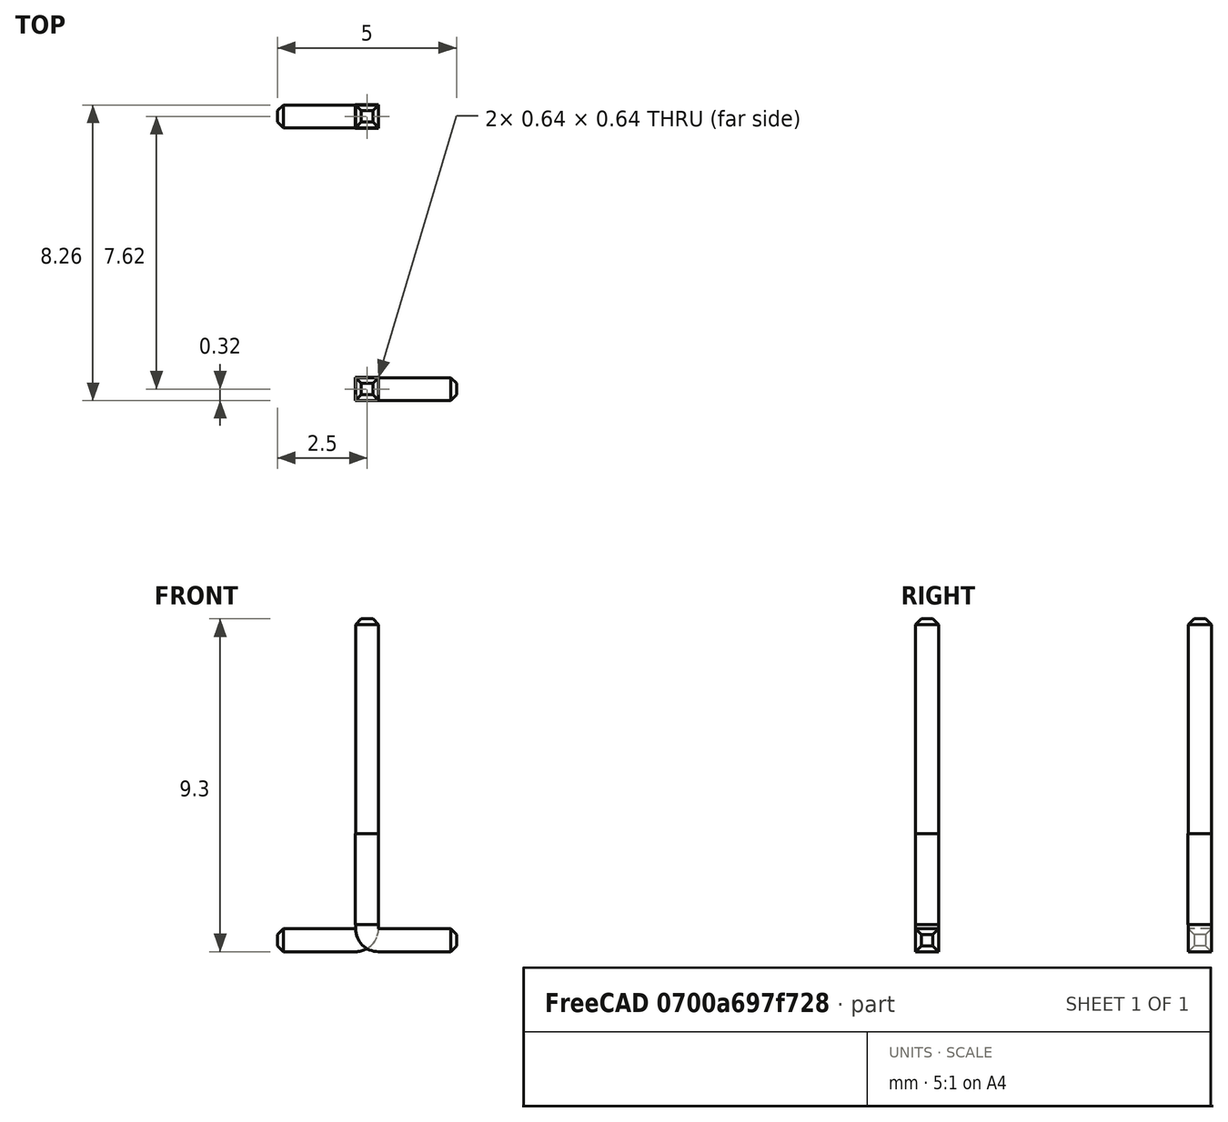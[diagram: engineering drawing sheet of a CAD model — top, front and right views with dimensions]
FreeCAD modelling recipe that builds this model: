
FCSTD DOCUMENT  (FreeCAD 0.16R6712 (Git))
Label: Pin_Neo
License: All rights reserved
LicenseURL: http://en.wikipedia.org/wiki/All_rights_reserved
objects: Part::Box×5, Part::Cut×5, Part::Feature×1, Part::FeaturePython×1
note: 12 computed .brp shape members not serialized (recipe doc carries the construction recipe); baked Part::Feature solids carry a one-line shape summary decoded from their .brp

FEATURE [Part::Feature] Part__Feature  label="PinHeader_1x04_P254mm_Vertical_SMD_Pin1Left"
  shape: bbox 5 x 10.16 x 9.3 mm, 112 faces (baked)
FEATURE [Part::Box] Box  label="Cube"
  Height = 12
  Length = 8
  Placement = pos=(-4,-3.48,-1) rot=(0,0,1;0rad)
  Width = 6.96
FEATURE [Part::Cut] Cut
  Base = -> Part__Feature
  Tool = -> Box
FEATURE [Part::FeaturePython] Clone  label="Clone of Cut"  # Draft clone (typed FeaturePython)
  Objects = -> [Cut]
  Scale = (1,1,1)
FEATURE [Part::Box] Box001  label="Cube001"
  Height = 10
  Length = 1.2
  Placement = pos=(0.321,-6,0.65) rot=(0,0,1;0rad)
  Width = 12
FEATURE [Part::Box] Box002  label="Cube002"
  Height = 10
  Length = 1.2
  Placement = pos=(-1.529,-6,0.65) rot=(0,0,1;0rad)
  Width = 12
FEATURE [Part::Box] Box003  label="Cube003"
  Height = 10
  Length = 3
  Placement = pos=(-1.529,-6,0.65) rot=(0,0,1;0rad)
  Width = 1.868
FEATURE [Part::Box] Box004  label="Cube004"
  Height = 10
  Length = 3
  Placement = pos=(-1.529,4.134,0.4) rot=(0,0,1;0rad)
  Width = 1.868
FEATURE [Part::Cut] Cut001
  Base = -> Clone
  Tool = -> Box001
FEATURE [Part::Cut] Cut002
  Base = -> Cut001
  Tool = -> Box002
FEATURE [Part::Cut] Cut003
  Base = -> Cut002
  Tool = -> Box003
FEATURE [Part::Cut] Cut004
  Base = -> Cut003
  Tool = -> Box004
